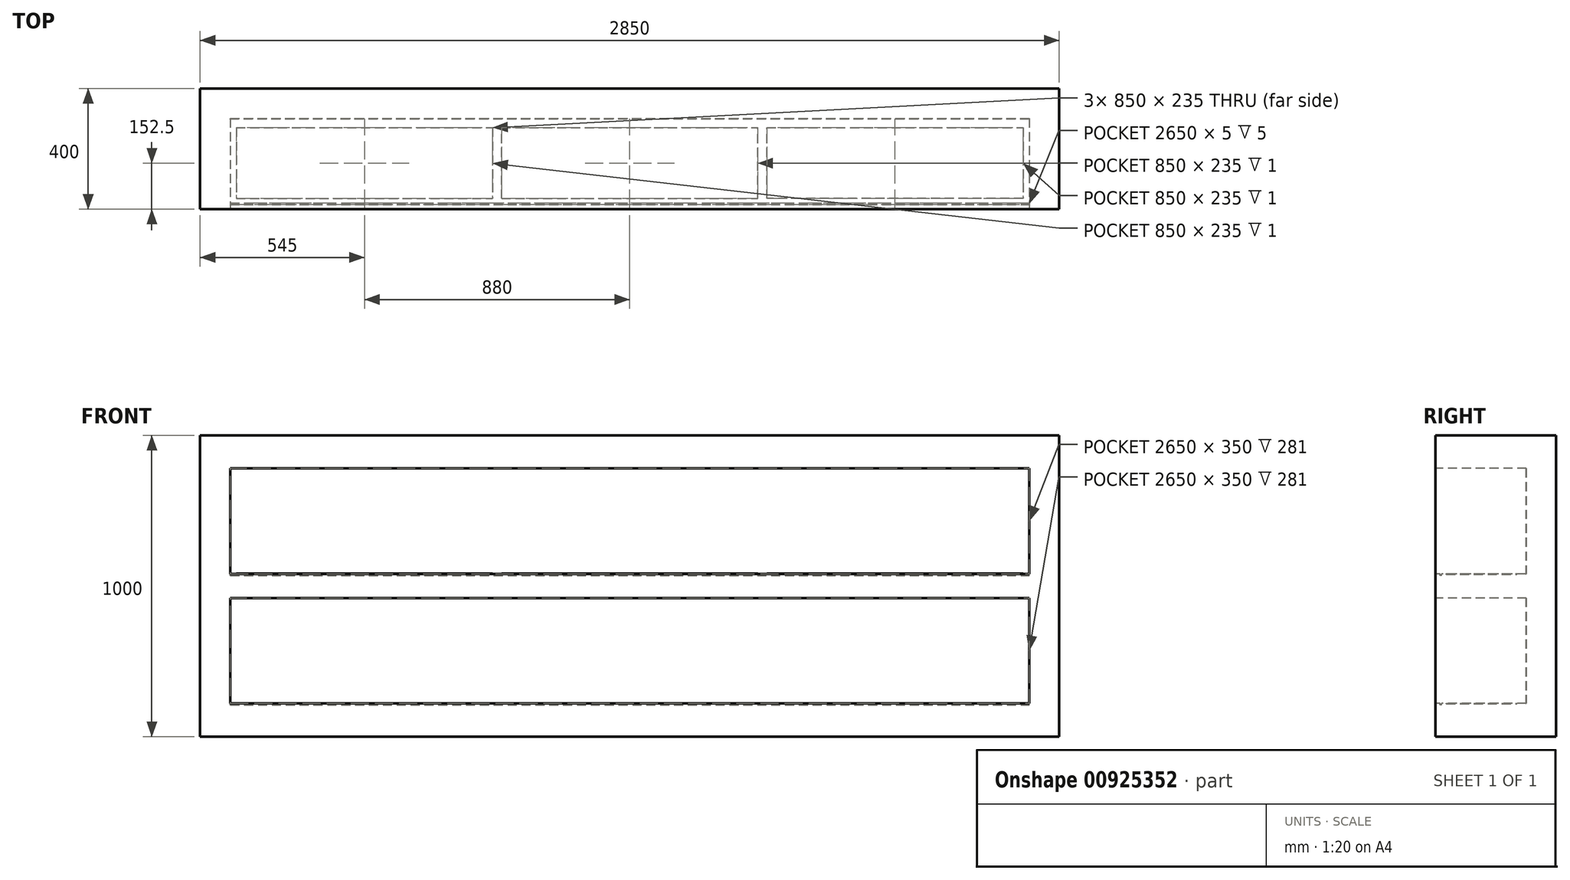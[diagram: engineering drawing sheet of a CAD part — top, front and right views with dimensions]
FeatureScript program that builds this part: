
annotation { "Feature Type Name" : "Feature", "Feature Type Description" : "" }
export const myFeature = defineFeature(function(context is Context, id is Id, definition is map)
    precondition{}
    {
        {
            var Q0;
            Q0=qCreatedBy(makeId("Front.planeOp"),FACE);
            var sketch = newSketch(context, id + "F0", { "sketchPlane" : qUnion([Q0])});
            skLineSegment(sketch, "E0.bottom", {"start": v(1425, -500) * mm, "end": v(-1425, -500) * mm});
            skLineSegment(sketch, "E0.top", {"start": v(1425, 500) * mm, "end": v(-1425, 500) * mm});
            skLineSegment(sketch, "E0.left", {"start": v(1425, -500) * mm, "end": v(1425, 500) * mm});
            skLineSegment(sketch, "E0.right", {"start": v(-1425, -500) * mm, "end": v(-1425, 500) * mm});
            skPoint(sketch, "E0.middle", {"position": v(0, 0) * mm});
            skSolve(sketch);
        }
        {
            var Q0;
            Q0 = qSketchRegion(id + "F0", true);
            extrude(context, id + "F1", {"entities" : qUnion([Q0]), "oppositeDirection" : true, "depth" : 400 * mm, "offsetDistance" : 25 * mm});
        }
        {
            var Q0;
            Q0=qCreatedBy(makeId("Front.planeOp"),FACE);
            var sketch = newSketch(context, id + "F2", { "sketchPlane" : qUnion([Q0])});
            skLineSegment(sketch, "E1.bottom", {"start": v(-1325, 390) * mm, "end": v(1325, 390) * mm});
            skLineSegment(sketch, "E1.top", {"start": v(-1325, 40) * mm, "end": v(1325, 40) * mm});
            skLineSegment(sketch, "E1.left", {"start": v(-1325, 390) * mm, "end": v(-1325, 40) * mm});
            skLineSegment(sketch, "E1.right", {"start": v(1325, 390) * mm, "end": v(1325, 40) * mm});
            skLineSegment(sketch, "E2.bottom", {"start": v(-1325, -40) * mm, "end": v(1325, -40) * mm});
            skLineSegment(sketch, "E2.top", {"start": v(-1325, -390) * mm, "end": v(1325, -390) * mm});
            skLineSegment(sketch, "E2.left", {"start": v(-1325, -40) * mm, "end": v(-1325, -390) * mm});
            skLineSegment(sketch, "E2.right", {"start": v(1325, -40) * mm, "end": v(1325, -390) * mm});
            skLineSegment(sketch, "E3", {"start": v(0, 0) * mm, "end": v(1687.6, 0) * mm, "construction": true});
            skLineSegment(sketch, "E4", {"start": v(0, 0) * mm, "end": v(0, 601.09) * mm, "construction": true});
            skSolve(sketch);
        }
        {
            var Q0;
            Q0 = qSketchRegion(id + "F2", true);
            extrude(context, id + "F3", {"entities" : qUnion([Q0]), "operationType" : NewBodyOperationType.REMOVE, "oppositeDirection" : true, "depth" : 300 * mm, "offsetDistance" : 25 * mm});
        }
        {
            var Q0;
            Q0=makeQuery(id+"F3.boolean.opBoolean","COPY",FACE,{"derivedFrom":makeQuery(id+"F3.opExtrude","SWEPT_FACE",FACE,{"disambiguationData":[OSD([sQuery(id+"F2.wireOp",EDGE,"E1.top")])]})});
            var sketch = newSketch(context, id + "F4", { "sketchPlane" : qUnion([Q0])});
            skLineSegment(sketch, "E5.bottom", {"start": v(-1325, 20) * mm, "end": v(1325, 20) * mm});
            skLineSegment(sketch, "E5.top", {"start": v(-1325, 15) * mm, "end": v(1325, 15) * mm});
            skLineSegment(sketch, "E5.left", {"start": v(-1325, 20) * mm, "end": v(-1325, 15) * mm});
            skLineSegment(sketch, "E5.right", {"start": v(1325, 20) * mm, "end": v(1325, 15) * mm});
            skSolve(sketch);
        }
        {
            var Q0;
            Q0 = qSketchRegion(id + "F4", true);
            extrude(context, id + "F5", {"entities" : qUnion([Q0]), "operationType" : NewBodyOperationType.REMOVE, "oppositeDirection" : true, "depth" : 5 * mm, "offsetDistance" : 25 * mm});
        }
        {
            var Q0;
            {var subQ2=sQuery(id+"F2.wireOp",EDGE,"E1.top");Q0=makeQuery(id+"F5.boolean.opBoolean","SPLIT",FACE,{"disambiguationData":[TD([makeQuery(id+"F5.opExtrude","SWEPT_FACE",FACE,{"disambiguationData":[OSD([sQuery(id+"F4.wireOp",EDGE,"E5.bottom")])]})])],"derivedFrom":makeQuery(id+"F3.boolean.opBoolean","COPY",FACE,{"derivedFrom":makeQuery(id+"F3.opExtrude","SWEPT_FACE",FACE,{"disambiguationData":[OSD([subQ2])]})})});}
            var sketch = newSketch(context, id + "F6", { "sketchPlane" : qUnion([Q0])});
            skLineSegment(sketch, "E6.bottom", {"start": v(-1305, 270) * mm, "end": v(-455, 270) * mm});
            skLineSegment(sketch, "E6.top", {"start": v(-1305, 35) * mm, "end": v(-455, 35) * mm});
            skLineSegment(sketch, "E6.left", {"start": v(-1305, 270) * mm, "end": v(-1305, 35) * mm});
            skLineSegment(sketch, "E6.right", {"start": v(-455, 270) * mm, "end": v(-455, 35) * mm});
            skLineSegment(sketch, "E7.bottom", {"start": v(455, 270) * mm, "end": v(1305, 270) * mm});
            skLineSegment(sketch, "E8", {"start": v(0, 0) * mm, "end": v(0, 930.5) * mm, "construction": true});
            skLineSegment(sketch, "E9.bottom", {"start": v(-425, 35) * mm, "end": v(425, 35) * mm});
            skLineSegment(sketch, "E9.top", {"start": v(-425, 270) * mm, "end": v(425, 270) * mm});
            skLineSegment(sketch, "E9.left", {"start": v(-425, 35) * mm, "end": v(-425, 270) * mm});
            skLineSegment(sketch, "E9.right", {"start": v(425, 35) * mm, "end": v(425, 270) * mm});
            skLineSegment(sketch, "E10", {"start": v(1305, 270) * mm, "end": v(1305, 35) * mm});
            skLineSegment(sketch, "E11", {"start": v(1305, 35) * mm, "end": v(455, 35) * mm});
            skLineSegment(sketch, "E12", {"start": v(455, 35) * mm, "end": v(455, 270) * mm});
            skSolve(sketch);
        }
        {
            var Q0;
            Q0 = qSketchRegion(id + "F6", true);
            extrude(context, id + "F7", {"entities" : qUnion([Q0]), "operationType" : NewBodyOperationType.REMOVE, "oppositeDirection" : true, "depth" : 1 * mm, "offsetDistance" : 25 * mm});
        }
        {
            var Q0;
            Q0=makeQuery(id+"F3.boolean.opBoolean","COPY",FACE,{"derivedFrom":makeQuery(id+"F3.opExtrude","SWEPT_FACE",FACE,{"disambiguationData":[OSD([sQuery(id+"F2.wireOp",EDGE,"E2.top")])]})});
            var sketch = newSketch(context, id + "F8", { "sketchPlane" : qUnion([Q0])});
            skLineSegment(sketch, "E13.bottom", {"start": v(-1325, 20) * mm, "end": v(1325, 20) * mm});
            skLineSegment(sketch, "E13.top", {"start": v(-1325, 15) * mm, "end": v(1325, 15) * mm});
            skLineSegment(sketch, "E13.left", {"start": v(-1325, 20) * mm, "end": v(-1325, 15) * mm});
            skLineSegment(sketch, "E13.right", {"start": v(1325, 20) * mm, "end": v(1325, 15) * mm});
            skSolve(sketch);
        }
        {
            var Q0;
            Q0 = qSketchRegion(id + "F8", true);
            extrude(context, id + "F9", {"entities" : qUnion([Q0]), "operationType" : NewBodyOperationType.REMOVE, "oppositeDirection" : true, "depth" : 5 * mm, "offsetDistance" : 25 * mm});
        }
        {
            var Q0;
            {var subQ2=sQuery(id+"F2.wireOp",EDGE,"E2.top");Q0=makeQuery(id+"F9.boolean.opBoolean","SPLIT",FACE,{"disambiguationData":[TD([makeQuery(id+"F9.opExtrude","SWEPT_FACE",FACE,{"disambiguationData":[OSD([sQuery(id+"F8.wireOp",EDGE,"E13.bottom")])]})])],"derivedFrom":makeQuery(id+"F3.boolean.opBoolean","COPY",FACE,{"derivedFrom":makeQuery(id+"F3.opExtrude","SWEPT_FACE",FACE,{"disambiguationData":[OSD([subQ2])]})})});}
            var sketch = newSketch(context, id + "F10", { "sketchPlane" : qUnion([Q0])});
            skLineSegment(sketch, "E14.0", {"start": v(-1305, 270) * mm, "end": v(-455, 270) * mm});
            skLineSegment(sketch, "E14.1", {"start": v(-1305, 35) * mm, "end": v(-455, 35) * mm});
            skLineSegment(sketch, "E14.2", {"start": v(-1305, 270) * mm, "end": v(-1305, 35) * mm});
            skLineSegment(sketch, "E14.3", {"start": v(-455, 270) * mm, "end": v(-455, 35) * mm});
            skLineSegment(sketch, "E14.4", {"start": v(455, 270) * mm, "end": v(1305, 270) * mm});
            skLineSegment(sketch, "E14.5", {"start": v(0, 0) * mm, "end": v(0, 930.5) * mm});
            skLineSegment(sketch, "E14.6", {"start": v(-425, 35) * mm, "end": v(425, 35) * mm});
            skLineSegment(sketch, "E14.7", {"start": v(-425, 270) * mm, "end": v(425, 270) * mm});
            skLineSegment(sketch, "E14.8", {"start": v(-425, 35) * mm, "end": v(-425, 270) * mm});
            skLineSegment(sketch, "E14.9", {"start": v(425, 35) * mm, "end": v(425, 270) * mm});
            skLineSegment(sketch, "E14.10", {"start": v(1305, 270) * mm, "end": v(1305, 35) * mm});
            skLineSegment(sketch, "E14.11", {"start": v(1305, 35) * mm, "end": v(455, 35) * mm});
            skLineSegment(sketch, "E14.12", {"start": v(455, 35) * mm, "end": v(455, 270) * mm});
            skSolve(sketch);
        }
        {
            var Q0;
            Q0 = qSketchRegion(id + "F10", true);
            extrude(context, id + "F11", {"entities" : qUnion([Q0]), "operationType" : NewBodyOperationType.REMOVE, "oppositeDirection" : true, "depth" : 1 * mm, "offsetDistance" : 25 * mm});
        }
        {
            var Q0;
            Q0 = qSketchRegion(id + "F10", true);
            extrude(context, id + "F12", {"entities" : qUnion([Q0]), "depth" : 1 * mm, "offsetDistance" : 25 * mm});
        }
        {
            var Q0;
            Q0 = qSketchRegion(id + "F6", true);
            extrude(context, id + "F13", {"entities" : qUnion([Q0]), "depth" : 1 * mm, "offsetDistance" : 25 * mm});
        }
        {
            var Q0;
            Q0=makeQuery(id+"F3.boolean.opBoolean","COPY",FACE,{"derivedFrom":makeQuery(id+"F3.opExtrude","CAP_FACE",FACE,{"disambiguationData":[OSD([sQuery(id+"F2.wireOp",EDGE,"E1.bottom"),sQuery(id+"F2.wireOp",EDGE,"E1.top"),sQuery(id+"F2.wireOp",EDGE,"E1.left"),sQuery(id+"F2.wireOp",EDGE,"E1.right")])],"isStart":false})});
            var sketch = newSketch(context, id + "F14", { "sketchPlane" : qUnion([Q0])});
            skLineSegment(sketch, "E15.1.0", {"start": v(-1325, -40) * mm, "end": v(-1325, -390) * mm});
            skLineSegment(sketch, "E15.1.1", {"start": v(-1325, -390) * mm, "end": v(1325, -390) * mm});
            skLineSegment(sketch, "E15.1.2", {"start": v(1325, -390) * mm, "end": v(1325, -40) * mm});
            skLineSegment(sketch, "E15.1.3", {"start": v(1325, -40) * mm, "end": v(-1325, -40) * mm});
            skLineSegment(sketch, "E16.0", {"start": v(-1325, 390) * mm, "end": v(1325, 390) * mm});
            skLineSegment(sketch, "E16.1", {"start": v(-1325, 390) * mm, "end": v(-1325, 40) * mm});
            skLineSegment(sketch, "E16.2", {"start": v(-1325, 40) * mm, "end": v(1325, 40) * mm});
            skLineSegment(sketch, "E16.3", {"start": v(1325, 390) * mm, "end": v(1325, 40) * mm});
            skSolve(sketch);
        }
        {
            var Q0;
            Q0 = qSketchRegion(id + "F14", true);
            extrude(context, id + "F15", {"entities" : qUnion([Q0]), "operationType" : NewBodyOperationType.REMOVE, "oppositeDirection" : true, "depth" : 1 * mm, "offsetDistance" : 25 * mm});
        }
        {
            var Q0;
            Q0 = qSketchRegion(id + "F14", true);
            extrude(context, id + "F16", {"entities" : qUnion([Q0]), "depth" : 1 * mm, "offsetDistance" : 25 * mm});
        }
    });
